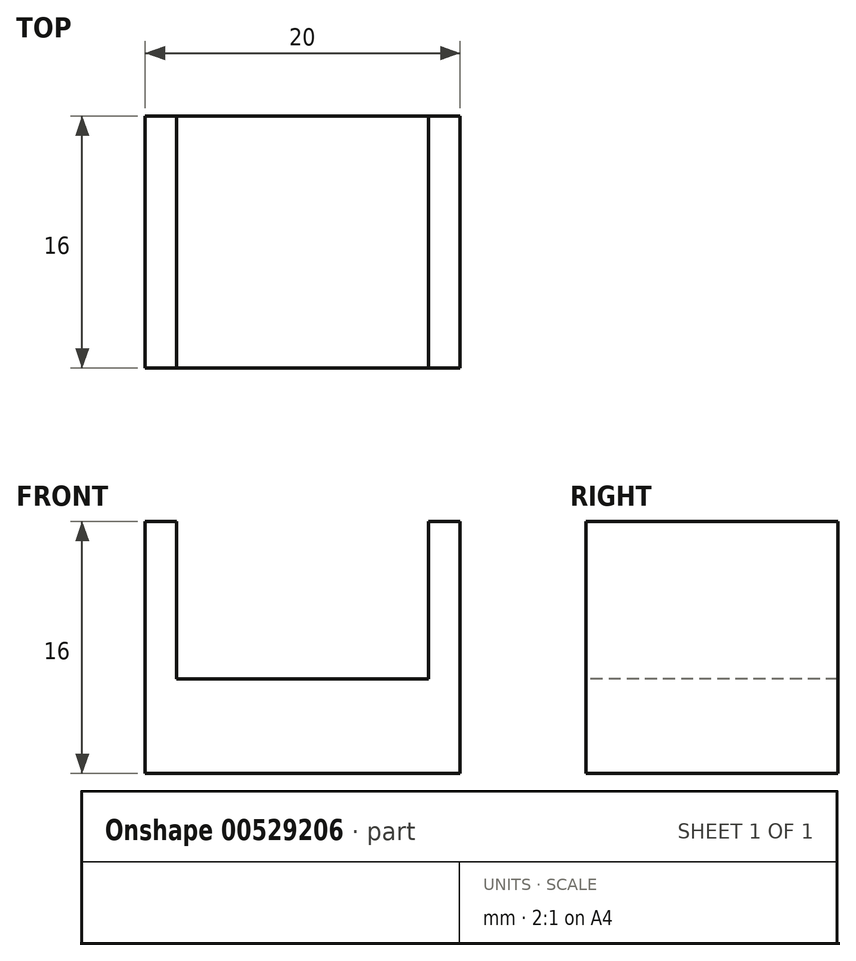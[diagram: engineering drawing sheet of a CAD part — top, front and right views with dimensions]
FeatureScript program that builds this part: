
annotation { "Feature Type Name" : "Feature", "Feature Type Description" : "" }
export const myFeature = defineFeature(function(context is Context, id is Id, definition is map)
    precondition{}
    {
        {
            var Q0;
            Q0=qCreatedBy(makeId("Top.planeOp"),FACE);
            var sketch = newSketch(context, id + "F0", { "sketchPlane" : qUnion([Q0])});
            skLineSegment(sketch, "E0.bottom", {"start": v(-66.86, -0.51) * mm, "end": v(-50.86, -0.51) * mm});
            skLineSegment(sketch, "E0.top", {"start": v(-66.86, -16.51) * mm, "end": v(-50.86, -16.51) * mm});
            skLineSegment(sketch, "E0.left", {"start": v(-66.86, -0.51) * mm, "end": v(-66.86, -16.51) * mm});
            skLineSegment(sketch, "E0.right", {"start": v(-50.86, -0.51) * mm, "end": v(-50.86, -16.51) * mm});
            skLineSegment(sketch, "E1.bottom", {"start": v(-68.86, -0.51) * mm, "end": v(-48.86, -0.51) * mm});
            skLineSegment(sketch, "E1.top", {"start": v(-68.86, -16.51) * mm, "end": v(-48.86, -16.51) * mm});
            skLineSegment(sketch, "E1.left", {"start": v(-68.86, -0.51) * mm, "end": v(-68.86, -16.51) * mm});
            skLineSegment(sketch, "E1.right", {"start": v(-48.86, -0.51) * mm, "end": v(-48.86, -16.51) * mm});
            skLineSegment(sketch, "E2", {"start": v(-68.86, -0.51) * mm, "end": v(-48.86, -16.51) * mm, "construction": true});
            skLineSegment(sketch, "E3", {"start": v(-68.86, -16.51) * mm, "end": v(-48.86, -0.51) * mm, "construction": true});
            skLineSegment(sketch, "E4", {"start": v(-66.86, -0.51) * mm, "end": v(-50.86, -16.51) * mm, "construction": true});
            skLineSegment(sketch, "E5", {"start": v(-66.86, -16.51) * mm, "end": v(-50.86, -0.51) * mm, "construction": true});
            skSolve(sketch);
        }
        {
            var Q0;
            {var subQ0=sQuery(id+"F0.wireOp",EDGE,"E0.left");Q0=makeQuery(id+"F0.imprint","IMPRINT",FACE,{"disambiguationData":[TD([[makeQuery(id+"F0.imprint","IMPRINT",EDGE,{"derivedFrom":subQ0}),1.0]])]});}
            var Q1;
            {var subQ0=sQuery(id+"F0.wireOp",EDGE,"E0.left");Q1=makeQuery(id+"F0.imprint","IMPRINT",FACE,{"disambiguationData":[TD([[makeQuery(id+"F0.imprint","IMPRINT",EDGE,{"derivedFrom":subQ0}),-1.0]])]});}
            var Q2;
            {var subQ0=sQuery(id+"F0.wireOp",EDGE,"E0.right");Q2=makeQuery(id+"F0.imprint","IMPRINT",FACE,{"disambiguationData":[TD([[makeQuery(id+"F0.imprint","IMPRINT",EDGE,{"derivedFrom":subQ0}),1.0]])]});}
            extrude(context, id + "F1", {"entities" : qUnion([Q0, Q1, Q2]), "oppositeDirection" : true, "depth" : 6 * mm, "offsetDistance" : 25 * mm});
        }
        {
            var Q0;
            {var subQ0=sQuery(id+"F0.wireOp",EDGE,"E0.left");Q0=makeQuery(id+"F0.imprint","IMPRINT",FACE,{"disambiguationData":[TD([[makeQuery(id+"F0.imprint","IMPRINT",EDGE,{"derivedFrom":subQ0}),-1.0]])]});}
            var Q1;
            {var subQ0=sQuery(id+"F0.wireOp",EDGE,"E0.right");Q1=makeQuery(id+"F0.imprint","IMPRINT",FACE,{"disambiguationData":[TD([[makeQuery(id+"F0.imprint","IMPRINT",EDGE,{"derivedFrom":subQ0}),1.0]])]});}
            extrude(context, id + "F2", {"entities" : qUnion([Q0, Q1]), "operationType" : NewBodyOperationType.ADD, "depth" : 10 * mm, "offsetDistance" : 25 * mm});
        }
    });
